# Revit family: Deckel für 90 Vertikalbogen, steigend
name_source: partatom
category: Generic Models
revit_build: Autodesk Revit 2015 (Build: 20140606_1530(x64)
units: mm (PartAtom-declared; Revit-internal decimal feet)

## types (14) — shared parameters
Manufacturer = OBO Bettermann
URL = http://www.obo-bettermann.com

## per-type parameters (varying)
| type | GTIN | Manufacturer Art.No. | Material | Width | Width 1 |
| DBV 100 S FS | 4012195047568 | 7130805 | Strip-galvanised | 100 mm  [stored 0.328084 ft] | 50 mm  [stored 0.164042 ft] |
| DBV 150 S FS | 4012195047575 | 7130809 | Strip-galvanised | 150 mm | 75 mm |
| DBV 200 S FS | 4012195047582 | 7130813 | Strip-galvanised | 200 mm  [stored 0.656168 ft] | 100 mm  [stored 0.328084 ft] |
| DBV 300 S FS | 4012195047612 | 7130817 | Strip-galvanised | 300 mm | 150 mm |
| DBV 400 S FS | 4012195047629 | 7130821 | Strip-galvanised | 400 mm  [stored 1.31234 ft] | 200 mm  [stored 0.656168 ft] |
| DBV 500 S FS | 4012195047636 | 7130825 | Strip-galvanised | 500 mm  [stored 1.64042 ft] | 250 mm  [stored 0.82021 ft] |
| DBV 600 S FS | 4012195047643 | 7130829 | Strip-galvanised | 600 mm | 300 mm |
| DBV 100 S DD | 4012195850915 | 7131508 | Strip galvanised zinc/aluminium, Double Dip | 100 mm  [stored 0.328084 ft] | 50 mm  [stored 0.164042 ft] |
| DBV 150 S DD | 4012195874386 | 7131509 | Strip galvanised zinc/aluminium, Double Dip | 150 mm | 75 mm |
| DBV 200 S DD | 4012195809265 | 7131510 | Strip galvanised zinc/aluminium, Double Dip | 200 mm  [stored 0.656168 ft] | 100 mm  [stored 0.328084 ft] |
| DBV 300 S DD | 4012195874393 | 7131514 | Strip galvanised zinc/aluminium, Double Dip | 300 mm | 150 mm |
| DBV 400 S DD | 4012195809272 | 7131518 | Strip galvanised zinc/aluminium, Double Dip | 400 mm  [stored 1.31234 ft] | 200 mm  [stored 0.656168 ft] |
| DBV 500 S DD | 4012195874409 | 7131524 | Strip galvanised zinc/aluminium, Double Dip | 500 mm  [stored 1.64042 ft] | 250 mm  [stored 0.82021 ft] |
| DBV 600 S DD | 4012195874416 | 7131527 | Strip galvanised zinc/aluminium, Double Dip | 600 mm | 300 mm |

note: column(s) folded — value = type name in every type: Article Type

note: [stored X ft] marks values corroborated as IEEE doubles in the binary element streams (Revit-internal decimal feet)

## geometry (parser evidence)
native form markers: Sweep x2
no freeform markers — native parametric forms only
